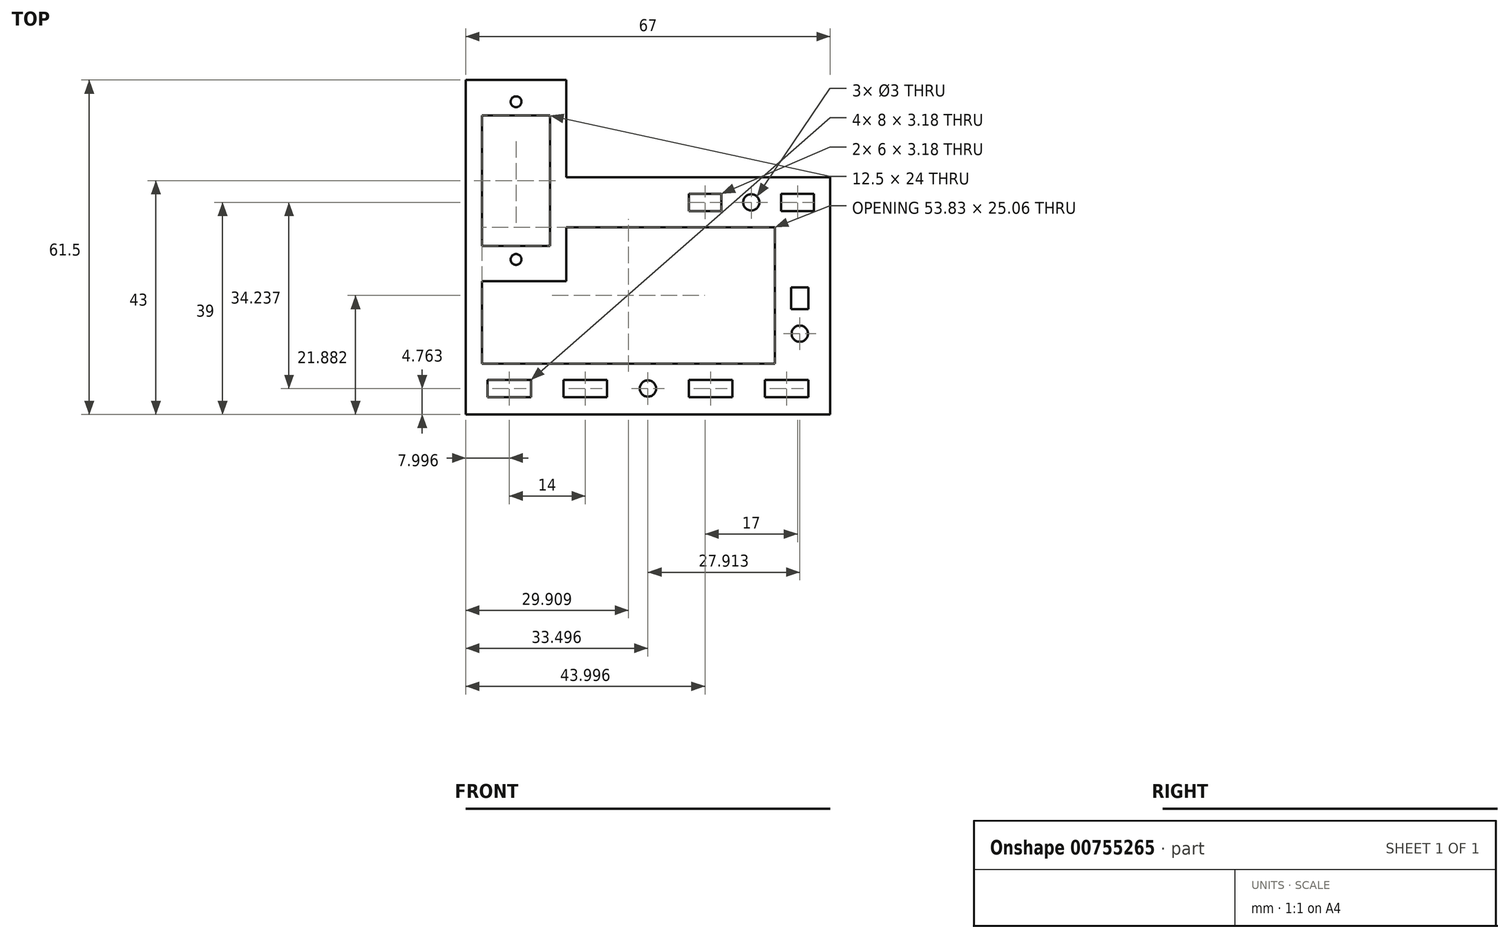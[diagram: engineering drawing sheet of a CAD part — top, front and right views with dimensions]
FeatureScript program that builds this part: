
annotation { "Feature Type Name" : "Feature", "Feature Type Description" : "" }
export const myFeature = defineFeature(function(context is Context, id is Id, definition is map)
    precondition{}
    {
        {
            var Q0;
            Q0=qCreatedBy(makeId("Top.planeOp"),FACE);
            var sketch = newSketch(context, id + "F0", { "sketchPlane" : qUnion([Q0])});
            skCircle(sketch, "E0", {"center": v(-7.56, -10.13) * mm, "radius": 1.5 * mm});
            skLineSegment(sketch, "E1.bottom", {"start": v(-0.06, -8.54) * mm, "end": v(7.94, -8.54) * mm});
            skLineSegment(sketch, "E1.top", {"start": v(-0.06, -11.71) * mm, "end": v(7.94, -11.71) * mm});
            skLineSegment(sketch, "E1.left", {"start": v(-0.06, -8.54) * mm, "end": v(-0.06, -11.71) * mm});
            skLineSegment(sketch, "E1.right", {"start": v(7.94, -8.54) * mm, "end": v(7.94, -11.71) * mm});
            skPoint(sketch, "E1.middle", {"position": v(3.94, -10.13) * mm});
            skLineSegment(sketch, "E2.MirrorCS", {"start": v(-15.06, -8.54) * mm, "end": v(-15.06, -11.71) * mm});
            skLineSegment(sketch, "E3.MirrorCS", {"start": v(-15.06, -8.54) * mm, "end": v(-23.06, -8.54) * mm});
            skLineSegment(sketch, "E4.MirrorCS", {"start": v(-15.06, -11.71) * mm, "end": v(-23.06, -11.71) * mm});
            skLineSegment(sketch, "E5.MirrorCS", {"start": v(-23.06, -8.54) * mm, "end": v(-23.06, -11.71) * mm});
            skLineSegment(sketch, "E6.bottom", {"start": v(13.94, -8.54) * mm, "end": v(21.94, -8.54) * mm});
            skLineSegment(sketch, "E6.top", {"start": v(13.94, -11.71) * mm, "end": v(21.94, -11.71) * mm});
            skLineSegment(sketch, "E6.left", {"start": v(13.94, -8.54) * mm, "end": v(13.94, -11.71) * mm});
            skLineSegment(sketch, "E6.right", {"start": v(21.94, -8.54) * mm, "end": v(21.94, -11.71) * mm});
            skLineSegment(sketch, "E7.bottom", {"start": v(-29.06, -8.54) * mm, "end": v(-37.06, -8.54) * mm});
            skLineSegment(sketch, "E7.top", {"start": v(-29.06, -11.71) * mm, "end": v(-37.06, -11.71) * mm});
            skLineSegment(sketch, "E7.left", {"start": v(-29.06, -8.54) * mm, "end": v(-29.06, -11.71) * mm});
            skLineSegment(sketch, "E7.right", {"start": v(-37.06, -8.54) * mm, "end": v(-37.06, -11.71) * mm});
            skLineSegment(sketch, "E8.bottom", {"start": v(-38.06, 40.11) * mm, "end": v(-25.56, 40.11) * mm});
            skLineSegment(sketch, "E8.top", {"start": v(-38.06, 16.11) * mm, "end": v(-25.56, 16.11) * mm});
            skLineSegment(sketch, "E8.left", {"start": v(-38.06, 40.11) * mm, "end": v(-38.06, 16.11) * mm});
            skLineSegment(sketch, "E8.right", {"start": v(-25.56, 40.11) * mm, "end": v(-25.56, 16.11) * mm});
            skPoint(sketch, "E8.middle", {"position": v(-31.81, 28.11) * mm});
            skCircle(sketch, "E9", {"center": v(-31.81, 42.61) * mm, "radius": 1 * mm});
            skCircle(sketch, "E10.MirrorC", {"center": v(-31.81, 13.61) * mm, "radius": 1 * mm});
            skCircle(sketch, "E11", {"center": v(11.44, 24.11) * mm, "radius": 1.5 * mm});
            skLineSegment(sketch, "E12.bottom", {"start": v(16.94, 25.7) * mm, "end": v(22.94, 25.7) * mm});
            skLineSegment(sketch, "E12.top", {"start": v(16.94, 22.52) * mm, "end": v(22.94, 22.52) * mm});
            skLineSegment(sketch, "E12.left", {"start": v(16.94, 25.7) * mm, "end": v(16.94, 22.52) * mm});
            skLineSegment(sketch, "E12.right", {"start": v(22.94, 25.7) * mm, "end": v(22.94, 22.52) * mm});
            skPoint(sketch, "E12.middle", {"position": v(19.94, 24.11) * mm});
            skLineSegment(sketch, "E13.MirrorCS", {"start": v(5.94, 25.7) * mm, "end": v(5.94, 22.52) * mm});
            skLineSegment(sketch, "E14.MirrorCS", {"start": v(5.94, 25.7) * mm, "end": v(-0.06, 25.7) * mm});
            skLineSegment(sketch, "E15.MirrorCS", {"start": v(-0.06, 25.7) * mm, "end": v(-0.06, 22.52) * mm});
            skLineSegment(sketch, "E16.MirrorCS", {"start": v(5.94, 22.52) * mm, "end": v(-0.06, 22.52) * mm});
            skLineSegment(sketch, "E17", {"start": v(-41.06, -14.89) * mm, "end": v(25.94, -14.89) * mm});
            skLineSegment(sketch, "E18", {"start": v(-41.06, -14.89) * mm, "end": v(-41.06, 46.61) * mm});
            skLineSegment(sketch, "E19", {"start": v(-41.06, 46.61) * mm, "end": v(-22.56, 46.61) * mm});
            skLineSegment(sketch, "E20", {"start": v(25.94, 28.7) * mm, "end": v(25.94, -14.89) * mm});
            skLineSegment(sketch, "E21", {"start": v(-7.56, -11.63) * mm, "end": v(-7.56, -14.89) * mm});
            skCircle(sketch, "E22", {"center": v(20.35, -0.04) * mm, "radius": 1.5 * mm});
            skLineSegment(sketch, "E23.bottom", {"start": v(18.76, 8.46) * mm, "end": v(21.94, 8.46) * mm});
            skLineSegment(sketch, "E23.top", {"start": v(18.76, 4.46) * mm, "end": v(21.94, 4.46) * mm});
            skLineSegment(sketch, "E23.left", {"start": v(18.76, 8.46) * mm, "end": v(18.76, 4.46) * mm});
            skLineSegment(sketch, "E23.right", {"start": v(21.94, 8.46) * mm, "end": v(21.94, 4.46) * mm});
            skPoint(sketch, "E23.middle", {"position": v(20.35, 6.46) * mm});
            skLineSegment(sketch, "E24", {"start": v(-22.56, 46.61) * mm, "end": v(-22.56, 28.7) * mm});
            skLineSegment(sketch, "E25", {"start": v(-22.56, 28.7) * mm, "end": v(25.94, 28.7) * mm});
            skLineSegment(sketch, "E26.bottom", {"start": v(-38.06, -5.54) * mm, "end": v(15.76, -5.54) * mm});
            skLineSegment(sketch, "E26.top", {"start": v(-38.06, 9.61) * mm, "end": v(-22.56, 9.61) * mm});
            skLineSegment(sketch, "E26.left", {"start": v(-38.06, -5.54) * mm, "end": v(-38.06, 9.61) * mm});
            skLineSegment(sketch, "E26.right", {"start": v(15.76, -5.54) * mm, "end": v(15.76, 9.61) * mm});
            skLineSegment(sketch, "E27.top", {"start": v(15.76, 19.52) * mm, "end": v(-22.56, 19.52) * mm});
            skLineSegment(sketch, "E27.left", {"start": v(15.76, 9.61) * mm, "end": v(15.76, 19.52) * mm});
            skLineSegment(sketch, "E27.right", {"start": v(-22.56, 9.61) * mm, "end": v(-22.56, 19.52) * mm});
            skPoint(sketch, "E28.end.orphan", {"position": v(-25.56, 28.11) * mm});
            skPoint(sketch, "E29.end.orphan", {"position": v(-31.81, 16.11) * mm});
            skSolve(sketch);
        }
        {
            var Q0;
            Q0=makeQuery(id+"F0.imprint","IMPRINT",FACE,{"disambiguationData":[TD([[makeQuery(id+"F0.imprint","IMPRINT",EDGE,{"derivedFrom":sQuery(id+"F0.wireOp",EDGE,"E1.bottom")}),1.0]])]});
            extrude(context, id + "F1", {"entities" : qUnion([Q0]), "depth" : 1 / 203.2 * mm, "offsetDistance" : 25 * mm});
        }
    });
